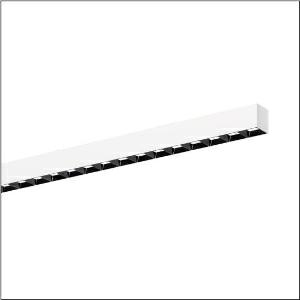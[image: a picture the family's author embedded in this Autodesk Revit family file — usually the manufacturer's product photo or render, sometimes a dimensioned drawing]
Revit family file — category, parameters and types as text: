
# Revit family: silica_r__21_51mx21tctaw_c13c
name_source: partatom
category: Lighting Fixtures
units: mm (PartAtom-declared; Revit-internal decimal feet)

## family parameters
Cut with Voids When Loaded = No
Host = Face
Light Source = No
Part Type = Normal
Room Calculation Point = No
Round Connector Dimension = Use Diameter
Shared = No

## types (1)
- --- (1 x LED, 9300 lm, 80.5 W, 6500K)
    Apparent Load = 81 VA
    CIE Flux Codes = 85 99 100 100 100
    Color Rendering = 80
    Color Temperature = 6500K
    Default Elevation = 1800 mm
    Description = Silica® 21, office luminaire, primary light control with darklight reflector, of PMMA, black, CAT 2 (L<= 3000cd/m²), light emission: direct distribution, primary light characteristic: symmetric, installation type: surface-mounted, LED, rated luminous flux: 9.300lm, luminous efficacy: 110lm/W, light colour: 8tw, colour temperature: 2700..6500K, control gear: ECG DALI, with terminal, 3+2-pole, max. 2.5mm², mains connection: 220..240V, AC, 50/60Hz, rated input power: 84.6W, luminaire housing, of aluminium, traffic white (RAL 9016), length: 3.004mm, width: 53mm, height: 53mm, protection rating (complete): IP20, insulation class (complete): insulation class I (protective earthing), certification: CE, permissible operating ambient temperature: 0..+35°C, standard: EN 50419, packaging unit: 1 piece
    Height = 0 mm  [stored 0 ft]
    Lamp = 1 x LED
    Lamp Light Flux = 9300 lm
    Lamp Power = 80.5 W
    Lamp count = 1
    Length = 3004 mm
    Luminous efficacy = 116 lm/W
    Manufacturer = Siteco
    ModVariant = No
    Model = 51MX21TCTAW
    Mounting Place = Ceiling
    Mounting Type = Recessed
    Number of Poles = 1
    OnlyDefault = Yes
    Power Factor = 1
    Product Name = Silica® 21
    Product group = office luminaire | ceiling recessed
    ProductGroupID = 400
    Protection Class = Protection class I
    Protection Degree = IP 20
    RLX_Detail_Level = 1
    RLX_Emergency_Light_Flux = 0 lm
    RLX_Emergency_Type = 0
    RLX_Emergency_Type_DB = No
    RlxData = <blob elided: 58805 chars, md5=c06254d2>
    Socket = socket
    Standby Power = 0 W
    System Light Flux = 9300 lm
    System Power = 81 W
    Type Comments = individual setting
    Type Image = l_1335873.jpg
    URL = http://relux.com
    VarID = @adj_109879
    Voltage = 0 V
    Weight = 0.00 kg
    Width = 53 mm

note: [stored X ft] marks values corroborated as IEEE doubles in the binary element streams (Revit-internal decimal feet)

## geometry (parser evidence)
native form markers: Blend x4, Sweep x11
no freeform markers — native parametric forms only
